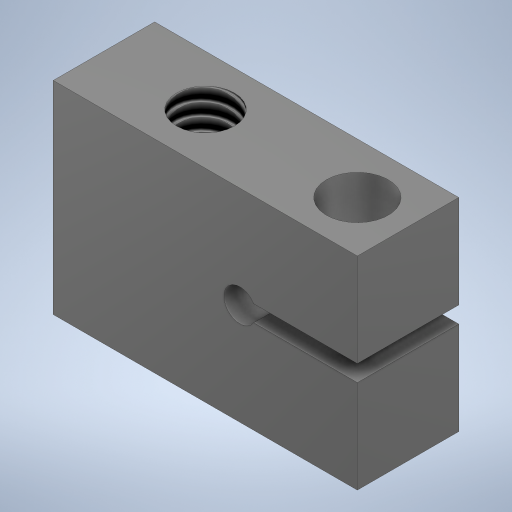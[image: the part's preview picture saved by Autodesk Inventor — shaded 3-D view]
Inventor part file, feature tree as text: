
AUTODESK INVENTOR PART (.ipt)
format: ipt  version: 2024 (Build 280153000, 153)  size: 250,368 bytes
history: native  units: in
note: dims shown in document units (in); Inventor stores cm internally (conversion verified against a paired STEP export)
features: other x3, thread x1
ambient origin geometry x8: Origin, YZ Plane, XZ Plane, XY Plane, X Axis, Y Axis, Z Axis, Center Point
bodies: Solid1 (feature_tree)
feature tree (4):
  other  "Drawing2.iam"
  other  "Drawing21.ipt:1"
  other  "Drawing24.ipt:1"
  thread  "Thread1"  [1 undecoded]
note: 1 required parameter value undecoded (feature->parameter linkage not recoverable at this tier; creation-order binding heuristic only, values carry confidence <= 0.55)
